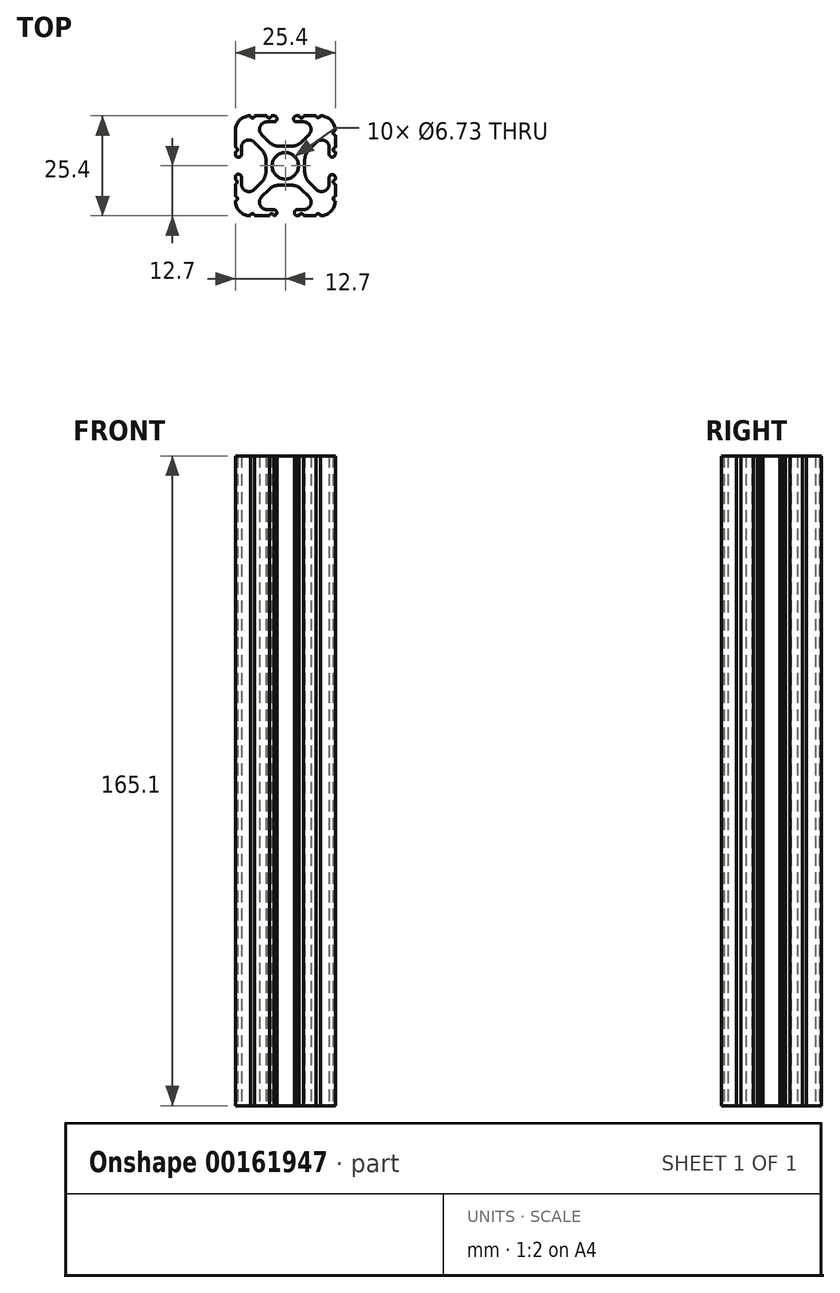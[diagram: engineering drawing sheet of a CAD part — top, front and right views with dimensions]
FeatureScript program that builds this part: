
annotation { "Feature Type Name" : "Feature", "Feature Type Description" : "" }
export const myFeature = defineFeature(function(context is Context, id is Id, definition is map)
    precondition{}
    {
        {
            var Q0;
            Q0=qCreatedBy(makeId("Top.planeOp"),FACE);
            var sketch = newSketch(context, id + "F0", { "sketchPlane" : qUnion([Q0])});
            skCircle(sketch, "E0", {"center": v(-12.7, 12.7) * mm, "radius": 3.36 * mm});
            skLineSegment(sketch, "E1.bottom", {"start": v(-11.24, 17.64) * mm, "end": v(-14.16, 17.64) * mm});
            skLineSegment(sketch, "E1.top", {"start": v(-11.24, 7.76) * mm, "end": v(-14.16, 7.76) * mm});
            skLineSegment(sketch, "E1.left", {"start": v(-7.76, 14.16) * mm, "end": v(-7.76, 11.24) * mm});
            skLineSegment(sketch, "E1.right", {"start": v(-17.64, 14.16) * mm, "end": v(-17.64, 11.24) * mm});
            skPoint(sketch, "E2.visualSharp", {"position": v(-25.4, 25.4) * mm});
            skPoint(sketch, "E3.visualSharp", {"position": v(0, 25.4) * mm});
            skPoint(sketch, "E4.visualSharp", {"position": v(0, 0) * mm});
            skPoint(sketch, "E5.visualSharp", {"position": v(-25.4, 0) * mm});
            skLineSegment(sketch, "E6.0", {"start": v(-18.7, 20.6) * mm, "end": v(-16.85, 18.76) * mm});
            skLineSegment(sketch, "E7.0", {"start": v(-20.6, 18.7) * mm, "end": v(-18.76, 16.85) * mm});
            skPoint(sketch, "E8.orphan", {"position": v(-23.85, 1.55) * mm});
            skPoint(sketch, "E9.orphan", {"position": v(-23.85, 23.85) * mm});
            skPoint(sketch, "E10.orphan", {"position": v(-1.55, 23.85) * mm});
            skPoint(sketch, "E11.orphan", {"position": v(-1.55, 1.55) * mm});
            skLineSegment(sketch, "E12", {"start": v(-8.55, 6.64) * mm, "end": v(-6.7, 4.8) * mm});
            skLineSegment(sketch, "E13.0", {"start": v(-18.7, 4.8) * mm, "end": v(-16.85, 6.64) * mm});
            skLineSegment(sketch, "E14.0", {"start": v(-20.6, 6.7) * mm, "end": v(-18.76, 8.55) * mm});
            skLineSegment(sketch, "E15.0", {"start": v(-8.55, 18.76) * mm, "end": v(-6.7, 20.6) * mm});
            skPoint(sketch, "E16.visualSharp", {"position": v(-23.85, 21.95) * mm});
            skArc(sketch, "E16.filletArc", {"start": v(-20.6, 18.7) * mm, "mid": v(-22.68, 19.1) * mm, "end": v(-23.85, 17.35) * mm});
            skPoint(sketch, "E17.visualSharp", {"position": v(-21.95, 23.85) * mm});
            skArc(sketch, "E17.filletArc", {"start": v(-17.35, 23.85) * mm, "mid": v(-19.1, 22.68) * mm, "end": v(-18.7, 20.6) * mm});
            skPoint(sketch, "E18.visualSharp", {"position": v(-5.34, 23.85) * mm});
            skLineSegment(sketch, "E19", {"start": v(-17.35, 23.85) * mm, "end": v(-15.58, 23.85) * mm});
            skLineSegment(sketch, "E20", {"start": v(-23.85, 17.35) * mm, "end": v(-23.85, 15.62) * mm});
            skLineSegment(sketch, "E21", {"start": v(-8.05, 1.55) * mm, "end": v(-9.78, 1.55) * mm});
            skArc(sketch, "E22.filletArc", {"start": v(-6.7, 20.6) * mm, "mid": v(-6.3, 22.68) * mm, "end": v(-8.05, 23.85) * mm});
            skPoint(sketch, "E23.visualSharp", {"position": v(-1.55, 3.45) * mm});
            skPoint(sketch, "E24.visualSharp", {"position": v(-3.45, 1.55) * mm});
            skArc(sketch, "E24.filletArc", {"start": v(-8.05, 1.55) * mm, "mid": v(-6.3, 2.73) * mm, "end": v(-6.7, 4.8) * mm});
            skArc(sketch, "E25.filletArc", {"start": v(-18.7, 4.8) * mm, "mid": v(-19.1, 2.73) * mm, "end": v(-17.35, 1.55) * mm});
            skArc(sketch, "E26.filletArc", {"start": v(-23.85, 8.05) * mm, "mid": v(-22.68, 6.3) * mm, "end": v(-20.6, 6.7) * mm});
            skLineSegment(sketch, "E27.bottom", {"start": v(-4.9, 0) * mm, "end": v(-8.05, 0) * mm});
            skLineSegment(sketch, "E27.top", {"start": v(-4.92, 25.4) * mm, "end": v(-8.05, 25.4) * mm});
            skLineSegment(sketch, "E27.left", {"start": v(0, 4.9) * mm, "end": v(0, 8.05) * mm});
            skLineSegment(sketch, "E27.right", {"start": v(-25.4, 4.9) * mm, "end": v(-25.4, 8.05) * mm});
            skArc(sketch, "E28.filletArc", {"start": v(-25.4, 3.81) * mm, "mid": v(-24.28, 1.12) * mm, "end": v(-21.59, 0) * mm});
            skArc(sketch, "E29.filletArc", {"start": v(-3.81, 0) * mm, "mid": v(-1.12, 1.12) * mm, "end": v(0, 3.8) * mm});
            skArc(sketch, "E30.filletArc", {"start": v(0, 21.59) * mm, "mid": v(-1.12, 24.28) * mm, "end": v(-3.8, 25.4) * mm});
            skArc(sketch, "E31.filletArc", {"start": v(-21.59, 25.4) * mm, "mid": v(-24.28, 24.28) * mm, "end": v(-25.4, 21.59) * mm});
            skPoint(sketch, "E32.newPointA", {"position": v(-17.64, 7.76) * mm});
            skArc(sketch, "E32.filletArc", {"start": v(-14.16, 7.76) * mm, "mid": v(-15.62, 7.47) * mm, "end": v(-16.85, 6.64) * mm});
            skPoint(sketch, "E33.newPointA", {"position": v(-7.76, 7.76) * mm});
            skArc(sketch, "E33.filletArc", {"start": v(-8.55, 6.64) * mm, "mid": v(-9.78, 7.47) * mm, "end": v(-11.24, 7.76) * mm});
            skArc(sketch, "E34.filletArc", {"start": v(-7.76, 11.24) * mm, "mid": v(-7.47, 9.78) * mm, "end": v(-6.64, 8.55) * mm});
            skArc(sketch, "E35.filletArc", {"start": v(-6.64, 16.85) * mm, "mid": v(-7.47, 15.62) * mm, "end": v(-7.76, 14.16) * mm});
            skPoint(sketch, "E36.newPointB", {"position": v(-7.76, 17.64) * mm});
            skArc(sketch, "E36.filletArc", {"start": v(-11.24, 17.64) * mm, "mid": v(-9.78, 17.93) * mm, "end": v(-8.55, 18.76) * mm});
            skPoint(sketch, "E37.newPointB", {"position": v(-17.64, 17.64) * mm});
            skArc(sketch, "E37.filletArc", {"start": v(-16.85, 18.76) * mm, "mid": v(-15.62, 17.93) * mm, "end": v(-14.16, 17.64) * mm});
            skArc(sketch, "E38.filletArc", {"start": v(-17.64, 14.16) * mm, "mid": v(-17.93, 15.62) * mm, "end": v(-18.76, 16.85) * mm});
            skArc(sketch, "E39.filletArc", {"start": v(-18.76, 8.55) * mm, "mid": v(-17.93, 9.78) * mm, "end": v(-17.64, 11.24) * mm});
            skLineSegment(sketch, "E40", {"start": v(-6.64, 8.55) * mm, "end": v(-4.8, 6.7) * mm});
            skPoint(sketch, "E41.visualSharp", {"position": v(-1.55, 21.95) * mm});
            skArc(sketch, "E42.filletArc", {"start": v(-4.8, 6.7) * mm, "mid": v(-2.73, 6.3) * mm, "end": v(-1.55, 8.05) * mm});
            skLineSegment(sketch, "E43", {"start": v(-1.55, 8.05) * mm, "end": v(-1.55, 9.78) * mm});
            skLineSegment(sketch, "E44", {"start": v(-6.64, 16.85) * mm, "end": v(-4.8, 18.7) * mm});
            skArc(sketch, "E45.filletArc", {"start": v(-1.55, 17.35) * mm, "mid": v(-2.73, 19.1) * mm, "end": v(-4.8, 18.7) * mm});
            skArc(sketch, "E46", {"start": v(-23.85, 9.78) * mm, "mid": v(-24.63, 10.56) * mm, "end": v(-25.4, 9.78) * mm});
            skArc(sketch, "E47", {"start": v(-25.4, 15.62) * mm, "mid": v(-24.63, 14.86) * mm, "end": v(-23.85, 15.62) * mm});
            skArc(sketch, "E48", {"start": v(-15.62, 23.85) * mm, "mid": v(-14.83, 24.63) * mm, "end": v(-15.62, 25.4) * mm});
            skArc(sketch, "E49", {"start": v(-9.78, 25.4) * mm, "mid": v(-10.6, 24.63) * mm, "end": v(-9.78, 23.85) * mm});
            skArc(sketch, "E50", {"start": v(-1.55, 15.62) * mm, "mid": v(-0.77, 14.88) * mm, "end": v(0, 15.62) * mm});
            skArc(sketch, "E51", {"start": v(0, 9.78) * mm, "mid": v(-0.77, 10.5) * mm, "end": v(-1.55, 9.78) * mm});
            skArc(sketch, "E52", {"start": v(-9.78, 1.55) * mm, "mid": v(-10.4, 0.77) * mm, "end": v(-9.78, 0) * mm});
            skArc(sketch, "E53", {"start": v(-15.62, 0) * mm, "mid": v(-14.85, 0.77) * mm, "end": v(-15.62, 1.55) * mm});
            skLineSegment(sketch, "E54.trimOffspring", {"start": v(-15.62, 1.55) * mm, "end": v(-17.35, 1.55) * mm});
            skLineSegment(sketch, "E55.trimOffspring", {"start": v(-16.7, 0) * mm, "end": v(-20.5, 0) * mm});
            skLineSegment(sketch, "E56.trimOffspring", {"start": v(-1.55, 15.62) * mm, "end": v(-1.55, 17.35) * mm});
            skLineSegment(sketch, "E57.trimOffspring", {"start": v(0, 15.62) * mm, "end": v(0, 16.26) * mm});
            skLineSegment(sketch, "E58.trimOffspring", {"start": v(-23.85, 9.78) * mm, "end": v(-23.85, 8.05) * mm});
            skLineSegment(sketch, "E59.trimOffspring", {"start": v(-25.4, 15.62) * mm, "end": v(-25.4, 16.26) * mm});
            skLineSegment(sketch, "E60.trimOffspring", {"start": v(-9.86, 23.85) * mm, "end": v(-8.05, 23.85) * mm});
            skLineSegment(sketch, "E61.trimOffspring", {"start": v(-15.58, 25.4) * mm, "end": v(-16.25, 25.4) * mm});
            skPoint(sketch, "E62.start.orphan", {"position": v(-15.62, 17.93) * mm});
            skPoint(sketch, "E63.start.orphan", {"position": v(-9.78, 17.93) * mm});
            skPoint(sketch, "E64.start.orphan", {"position": v(-7.47, 15.62) * mm});
            skPoint(sketch, "E65.start.orphan", {"position": v(-7.47, 9.78) * mm});
            skPoint(sketch, "E66.start.orphan", {"position": v(-17.93, 15.62) * mm});
            skPoint(sketch, "E67.start.orphan", {"position": v(-17.93, 9.78) * mm});
            skPoint(sketch, "E68.start.orphan", {"position": v(-9.78, 7.47) * mm});
            skPoint(sketch, "E69.start.orphan", {"position": v(-15.62, 7.47) * mm});
            skPoint(sketch, "E70.endSnap0", {"position": v(0, 18.6) * mm});
            skPoint(sketch, "E71.startSnap0", {"position": v(-1.55, 8.92) * mm});
            skArc(sketch, "E72", {"start": v(-4.92, 25.4) * mm, "mid": v(-4.37, 24.9) * mm, "end": v(-3.81, 25.4) * mm});
            skArc(sketch, "E73", {"start": v(-9.14, 25.4) * mm, "mid": v(-8.6, 24.86) * mm, "end": v(-8.05, 25.4) * mm});
            skArc(sketch, "E74", {"start": v(-17.35, 25.4) * mm, "mid": v(-16.8, 24.86) * mm, "end": v(-16.25, 25.4) * mm});
            skArc(sketch, "E75", {"start": v(-21.59, 25.4) * mm, "mid": v(-21.04, 24.85) * mm, "end": v(-20.49, 25.4) * mm});
            skLineSegment(sketch, "E76", {"start": v(-25.4, 21.59) * mm, "end": v(-25.4, 20.5) * mm});
            skArc(sketch, "E77", {"start": v(-25.4, 16.26) * mm, "mid": v(-24.84, 16.8) * mm, "end": v(-25.4, 17.35) * mm});
            skArc(sketch, "E78", {"start": v(-25.4, 8.05) * mm, "mid": v(-24.9, 8.6) * mm, "end": v(-25.4, 9.15) * mm});
            skArc(sketch, "E79", {"start": v(-25.4, 3.81) * mm, "mid": v(-24.85, 4.36) * mm, "end": v(-25.4, 4.9) * mm});
            skArc(sketch, "E80", {"start": v(-20.5, 0) * mm, "mid": v(-21.04, 0.55) * mm, "end": v(-21.59, 0) * mm});
            skArc(sketch, "E81", {"start": v(-15.62, 0) * mm, "mid": v(-16.16, 0.54) * mm, "end": v(-16.7, 0) * mm});
            skArc(sketch, "E82", {"start": v(-8.05, 0) * mm, "mid": v(-8.6, 0.55) * mm, "end": v(-9.15, 0) * mm});
            skArc(sketch, "E83", {"start": v(-3.81, 0) * mm, "mid": v(-4.35, 0.54) * mm, "end": v(-4.9, 0) * mm});
            skLineSegment(sketch, "E84.trimOffspring", {"start": v(-17.35, 25.4) * mm, "end": v(-20.49, 25.4) * mm});
            skLineSegment(sketch, "E85.trimOffspring", {"start": v(-25.4, 17.35) * mm, "end": v(-25.4, 21.59) * mm});
            skLineSegment(sketch, "E86.trimOffspring", {"start": v(-25.4, 9.15) * mm, "end": v(-25.4, 9.78) * mm});
            skLineSegment(sketch, "E87.trimOffspring", {"start": v(-9.15, 0) * mm, "end": v(-9.78, 0) * mm});
            skArc(sketch, "E88", {"start": v(0, 4.9) * mm, "mid": v(-0.54, 4.36) * mm, "end": v(0, 3.8) * mm});
            skArc(sketch, "E89", {"start": v(0, 9.15) * mm, "mid": v(-0.54, 8.6) * mm, "end": v(0, 8.05) * mm});
            skLineSegment(sketch, "E90.trimOffspring", {"start": v(0, 9.15) * mm, "end": v(0, 9.78) * mm});
            skArc(sketch, "E91", {"start": v(0, 21.59) * mm, "mid": v(-0.55, 21.04) * mm, "end": v(0, 20.5) * mm});
            skArc(sketch, "E92", {"start": v(0, 17.35) * mm, "mid": v(-0.55, 16.8) * mm, "end": v(0, 16.26) * mm});
            skLineSegment(sketch, "E93.trimOffspring", {"start": v(0, 17.35) * mm, "end": v(0, 20.5) * mm});
            skLineSegment(sketch, "E94.trimOffspring", {"start": v(-9.14, 25.4) * mm, "end": v(-9.86, 25.4) * mm});
            skSolve(sketch);
        }
        {
            var Q0;
            Q0=qSketchRegion(id+"F0",true);
            extrude(context, id + "F1", {"entities" : qUnion([Q0]), "depth" : 165.1 * mm});
        }
    });
